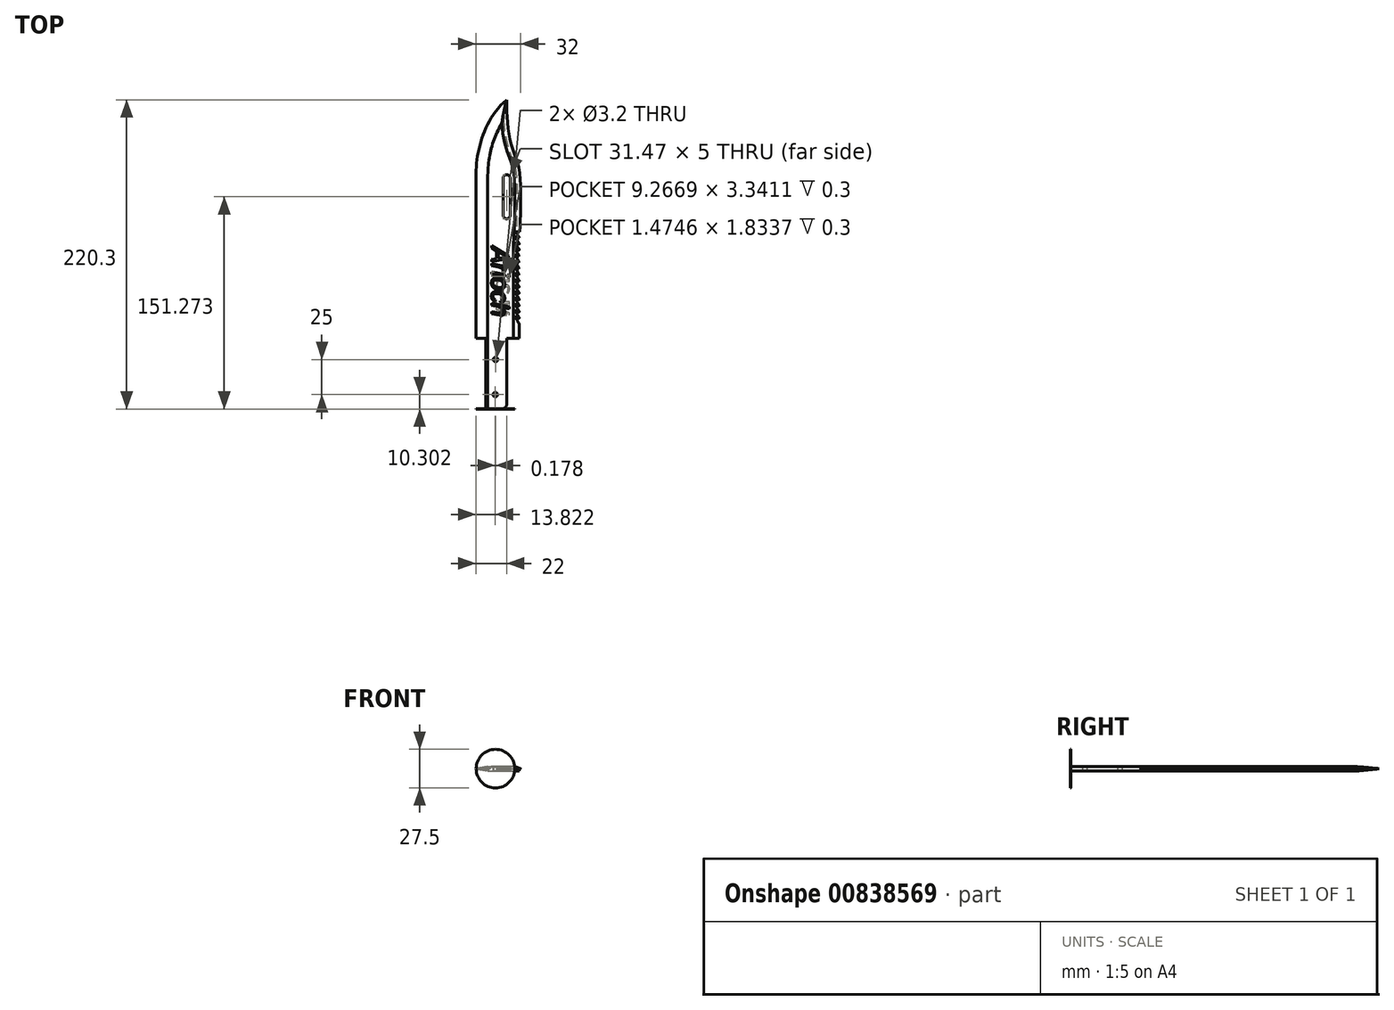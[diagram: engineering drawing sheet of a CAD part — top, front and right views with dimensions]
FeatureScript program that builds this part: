
annotation { "Feature Type Name" : "Feature", "Feature Type Description" : "" }
export const myFeature = defineFeature(function(context is Context, id is Id, definition is map)
    precondition{}
    {
        {
            var Q0;
            Q0=qCreatedBy(makeId("Top.planeOp"),FACE);
            var sketch = newSketch(context, id + "F0", { "sketchPlane" : qUnion([Q0])});
            skLineSegment(sketch, "E0", {"start": v(0, 138.73) * mm, "end": v(0, -81.27) * mm, "construction": true});
            skLineSegment(sketch, "E1", {"start": v(-22, -31.27) * mm, "end": v(9, -31.27) * mm, "construction": true});
            skLineSegment(sketch, "E2", {"start": v(-15, -31.27) * mm, "end": v(-15, -79.27) * mm});
            skLineSegment(sketch, "E3", {"start": v(0, -31.27) * mm, "end": v(0, -78.27) * mm});
            skLineSegment(sketch, "E4", {"start": v(-13, -81.27) * mm, "end": v(-3, -81.27) * mm});
            skPoint(sketch, "E5.visualSharp", {"position": v(0, -81.27) * mm});
            skArc(sketch, "E5.filletArc", {"start": v(-3, -81.27) * mm, "mid": v(-0.88, -80.39) * mm, "end": v(0, -78.27) * mm});
            skPoint(sketch, "E6.visualSharp", {"position": v(-15, -81.27) * mm});
            skArc(sketch, "E6.filletArc", {"start": v(-15, -79.27) * mm, "mid": v(-14.41, -80.68) * mm, "end": v(-13, -81.27) * mm});
            skLineSegment(sketch, "E7", {"start": v(9, -31.27) * mm, "end": v(9, 122.8) * mm, "construction": true});
            skLineSegment(sketch, "E8", {"start": v(-22, -31.27) * mm, "end": v(-22, 123.89) * mm, "construction": true});
            skLineSegment(sketch, "E9", {"start": v(-15, -31.27) * mm, "end": v(-22, -31.27) * mm});
            skLineSegment(sketch, "E10", {"start": v(0, -31.27) * mm, "end": v(9, -31.27) * mm});
            skLineSegment(sketch, "E11", {"start": v(-22, -31.27) * mm, "end": v(-22, 83.23) * mm});
            skFitSpline(sketch, "E12", {"points": [v(-22, 83.23) * mm, v(0, 138.73) * mm], "startDerivative": vector(0, 80.42) * mm, "endDerivative": vector(35.05, 28.76) * mm});
            skFitSpline(sketch, "E13", {"points": [v(0, 138.73) * mm, v(8.64, 90.14) * mm, v(9, 37.85) * mm, v(9, -31.27) * mm], "startDerivative": vector(0, -335.88) * mm, "endDerivative": vector(0, -393.77) * mm});
            skLineSegment(sketch, "E14", {"start": v(-8, -81.27) * mm, "end": v(-8, -31.27) * mm, "construction": true});
            skCircle(sketch, "E15", {"center": v(-8.18, -71.27) * mm, "radius": 1.6 * mm});
            skCircle(sketch, "E16", {"center": v(-8, -46.27) * mm, "radius": 1.6 * mm});
            skSolve(sketch);
        }
        {
            var Q0;
            Q0 = qSketchRegion(id + "F0", true);
            extrude(context, id + "F1", {"entities" : qUnion([Q0]), "depth" : 3 * mm, "offsetDistance" : 25.4 * mm});
        }
        {
            var Q0;
            Q0=makeQuery(id+"F1.opExtrude","CAP_EDGE",EDGE,{"disambiguationData":[OSD([sQuery(id+"F0.wireOp",EDGE,"E11")])],"isStart":false});
            var Q1;
            Q1=makeQuery(id+"F1.opExtrude","CAP_EDGE",EDGE,{"disambiguationData":[OSD([sQuery(id+"F0.wireOp",EDGE,"E12")])],"isStart":false});
            chamfer(context, id + "F2", {"entities" : qUnion([Q0, Q1]), "chamferType" : ChamferType.OFFSET_ANGLE, "width" : 1.5 * mm, "oppositeDirection" : false, "angle" : 80 * degree, "tangentPropagation" : true});
        }
        {
            var Q0;
            Q0=makeQuery(id+"F1.opExtrude","CAP_EDGE",EDGE,{"disambiguationData":[OSD([sQuery(id+"F0.wireOp",EDGE,"E12")])],"isStart":true});
            chamfer(context, id + "F3", {"entities" : qUnion([Q0]), "chamferType" : ChamferType.OFFSET_ANGLE, "width" : 1.5 * mm, "oppositeDirection" : true, "angle" : 80 * degree, "tangentPropagation" : true});
        }
        {
            var Q0;
            Q0=makeQuery(id+"F1.opExtrude","CAP_FACE",FACE,{"disambiguationData":[OSD([sQuery(id+"F0.wireOp",EDGE,"E2"),sQuery(id+"F0.wireOp",EDGE,"E3"),sQuery(id+"F0.wireOp",EDGE,"E4"),sQuery(id+"F0.wireOp",EDGE,"E5.filletArc"),sQuery(id+"F0.wireOp",EDGE,"E6.filletArc"),sQuery(id+"F0.wireOp",EDGE,"E9"),sQuery(id+"F0.wireOp",EDGE,"E10"),sQuery(id+"F0.wireOp",EDGE,"E11"),sQuery(id+"F0.wireOp",EDGE,"E12"),sQuery(id+"F0.wireOp",EDGE,"E13")])],"isStart":true});
            var sketch = newSketch(context, id + "F4", { "sketchPlane" : qUnion([Q0])});
            skSolve(sketch);
        }
        {
            var Q0;
            {var subQ3=sQuery(id+"F0.wireOp",EDGE,"E10");Q0=makeQuery(id+"F4.imprint","IMPRINT",FACE,{"disambiguationData":[TD([[makeQuery(id+"F4.imprint","IMPRINT",EDGE,{"derivedFrom":makeQuery(id+"F1.opExtrude","CAP_EDGE",EDGE,{"disambiguationData":[OSD([subQ3])],"isStart":true})}),-1.0]])]});}
            var sketch = newSketch(context, id + "F5", { "sketchPlane" : qUnion([Q0])});
            skLineSegment(sketch, "E17", {"start": v(10.09, 23.07) * mm, "end": v(6.53, 16.8) * mm});
            skLineSegment(sketch, "E18", {"start": v(6.53, 16.8) * mm, "end": v(10.43, 16.8) * mm});
            skLineSegment(sketch, "E19", {"start": v(10.09, 23.07) * mm, "end": v(10.43, 16.8) * mm});
            skLineSegment(sketch, "E20.0.1.0", {"start": v(10.09, 18.67) * mm, "end": v(10.43, 12.4) * mm});
            skLineSegment(sketch, "E20.0.1.1", {"start": v(6.53, 12.4) * mm, "end": v(10.43, 12.4) * mm});
            skLineSegment(sketch, "E20.0.1.2", {"start": v(10.09, 18.67) * mm, "end": v(6.53, 12.4) * mm});
            skLineSegment(sketch, "E20.0.2.0", {"start": v(10.09, 14.27) * mm, "end": v(10.43, 8) * mm});
            skLineSegment(sketch, "E20.0.2.1", {"start": v(6.53, 8) * mm, "end": v(10.43, 8) * mm});
            skLineSegment(sketch, "E20.0.2.2", {"start": v(10.09, 14.27) * mm, "end": v(6.53, 8) * mm});
            skLineSegment(sketch, "E20.0.3.0", {"start": v(10.09, 9.87) * mm, "end": v(10.43, 3.6) * mm});
            skLineSegment(sketch, "E20.0.3.1", {"start": v(6.53, 3.6) * mm, "end": v(10.43, 3.6) * mm});
            skLineSegment(sketch, "E20.0.3.2", {"start": v(10.09, 9.87) * mm, "end": v(6.53, 3.6) * mm});
            skLineSegment(sketch, "E20.0.4.0", {"start": v(10.09, 5.47) * mm, "end": v(10.43, -0.8) * mm});
            skLineSegment(sketch, "E20.0.4.1", {"start": v(6.53, -0.8) * mm, "end": v(10.43, -0.8) * mm});
            skLineSegment(sketch, "E20.0.4.2", {"start": v(10.09, 5.47) * mm, "end": v(6.53, -0.8) * mm});
            skLineSegment(sketch, "E20.0.5.0", {"start": v(10.09, 1.07) * mm, "end": v(10.43, -5.2) * mm});
            skLineSegment(sketch, "E20.0.5.1", {"start": v(6.53, -5.2) * mm, "end": v(10.43, -5.2) * mm});
            skLineSegment(sketch, "E20.0.5.2", {"start": v(10.09, 1.07) * mm, "end": v(6.53, -5.2) * mm});
            skLineSegment(sketch, "E20.0.6.0", {"start": v(10.09, -3.33) * mm, "end": v(10.43, -9.6) * mm});
            skLineSegment(sketch, "E20.0.6.1", {"start": v(6.53, -9.6) * mm, "end": v(10.43, -9.6) * mm});
            skLineSegment(sketch, "E20.0.6.2", {"start": v(10.09, -3.33) * mm, "end": v(6.53, -9.6) * mm});
            skLineSegment(sketch, "E20.0.7.0", {"start": v(10.09, -7.73) * mm, "end": v(10.43, -14) * mm});
            skLineSegment(sketch, "E20.0.7.1", {"start": v(6.53, -14) * mm, "end": v(10.43, -14) * mm});
            skLineSegment(sketch, "E20.0.7.2", {"start": v(10.09, -7.73) * mm, "end": v(6.53, -14) * mm});
            skLineSegment(sketch, "E20.0.8.0", {"start": v(10.09, -12.13) * mm, "end": v(10.43, -18.4) * mm});
            skLineSegment(sketch, "E20.0.8.1", {"start": v(6.53, -18.4) * mm, "end": v(10.43, -18.4) * mm});
            skLineSegment(sketch, "E20.0.8.2", {"start": v(10.09, -12.13) * mm, "end": v(6.53, -18.4) * mm});
            skLineSegment(sketch, "E20.0.9.0", {"start": v(10.09, -16.53) * mm, "end": v(10.43, -22.8) * mm});
            skLineSegment(sketch, "E20.0.9.1", {"start": v(6.53, -22.8) * mm, "end": v(10.43, -22.8) * mm});
            skLineSegment(sketch, "E20.0.9.2", {"start": v(10.09, -16.53) * mm, "end": v(6.53, -22.8) * mm});
            skLineSegment(sketch, "E20.direction1", {"start": v(6.53, 16.8) * mm, "end": v(32.82, 16.8) * mm, "construction": true});
            skLineSegment(sketch, "E20.direction2", {"start": v(6.53, 16.8) * mm, "end": v(6.53, 12.4) * mm, "construction": true});
            skLineSegment(sketch, "E21.0.0.10", {"start": v(10.09, -20.93) * mm, "end": v(10.43, -27.2) * mm});
            skLineSegment(sketch, "E21.3.0.10", {"start": v(6.53, -27.2) * mm, "end": v(10.43, -27.2) * mm});
            skLineSegment(sketch, "E21.6.0.10", {"start": v(10.09, -20.93) * mm, "end": v(6.53, -27.2) * mm});
            skLineSegment(sketch, "E21.0.0.11", {"start": v(10.09, -25.33) * mm, "end": v(10.43, -31.6) * mm});
            skLineSegment(sketch, "E21.3.0.11", {"start": v(6.53, -31.6) * mm, "end": v(10.43, -31.6) * mm});
            skLineSegment(sketch, "E21.6.0.11", {"start": v(10.09, -25.33) * mm, "end": v(6.53, -31.6) * mm});
            skLineSegment(sketch, "E21.0.0.12", {"start": v(10.09, -29.73) * mm, "end": v(10.43, -36) * mm});
            skLineSegment(sketch, "E21.3.0.12", {"start": v(6.53, -36) * mm, "end": v(10.43, -36) * mm});
            skLineSegment(sketch, "E21.6.0.12", {"start": v(10.09, -29.73) * mm, "end": v(6.53, -36) * mm});
            skLineSegment(sketch, "E21.0.0.13", {"start": v(10.09, -34.13) * mm, "end": v(10.43, -40.4) * mm});
            skLineSegment(sketch, "E21.3.0.13", {"start": v(6.53, -40.4) * mm, "end": v(10.43, -40.4) * mm});
            skLineSegment(sketch, "E21.6.0.13", {"start": v(10.09, -34.13) * mm, "end": v(6.53, -40.4) * mm});
            skLineSegment(sketch, "E21.0.0.14", {"start": v(10.09, -38.53) * mm, "end": v(10.43, -44.8) * mm});
            skLineSegment(sketch, "E21.3.0.14", {"start": v(6.53, -44.8) * mm, "end": v(10.43, -44.8) * mm});
            skLineSegment(sketch, "E21.6.0.14", {"start": v(10.09, -38.53) * mm, "end": v(6.53, -44.8) * mm});
            skSolve(sketch);
        }
        {
            var Q0;
            Q0 = qSketchRegion(id + "F5", true);
            extrude(context, id + "F6", {"entities" : qUnion([Q0]), "operationType" : NewBodyOperationType.REMOVE, "oppositeDirection" : true, "depth" : 25 * mm, "offsetDistance" : 25 * mm});
        }
        {
            var Q0;
            {var subQ3=sQuery(id+"F0.wireOp",EDGE,"E10");Q0=makeQuery(id+"F4.imprint","IMPRINT",FACE,{"disambiguationData":[TD([[makeQuery(id+"F4.imprint","IMPRINT",EDGE,{"derivedFrom":makeQuery(id+"F1.opExtrude","CAP_EDGE",EDGE,{"disambiguationData":[OSD([subQ3])],"isStart":true})}),-1.0]])]});}
            var sketch = newSketch(context, id + "F7", { "sketchPlane" : qUnion([Q0])});
            skLineSegment(sketch, "E22", {"start": v(0, -56.47) * mm, "end": v(0, -82.94) * mm, "construction": true});
            skArc(sketch, "E23.0.startCap", {"start": v(-2.5, -56.47) * mm, "mid": v(0, -53.97) * mm, "end": v(2.5, -56.47) * mm});
            skArc(sketch, "E23.0.endCap", {"start": v(2.5, -82.94) * mm, "mid": v(0, -85.44) * mm, "end": v(-2.5, -82.94) * mm});
            skLineSegment(sketch, "E23.0.left", {"start": v(2.5, -56.47) * mm, "end": v(2.5, -82.94) * mm});
            skLineSegment(sketch, "E23.0.right", {"start": v(-2.5, -56.47) * mm, "end": v(-2.5, -82.94) * mm});
            skSolve(sketch);
        }
        {
            var Q0;
            Q0 = qSketchRegion(id + "F7", true);
            extrude(context, id + "F8", {"entities" : qUnion([Q0]), "operationType" : NewBodyOperationType.REMOVE, "oppositeDirection" : true, "depth" : 25 * mm, "offsetDistance" : 25 * mm});
        }
        {
            var Q0;
            {var subQ0=sQuery(id+"F0.wireOp",EDGE,"E13");var subQ1=sQuery(id+"F0.wireOp",EDGE,"E12");Q0=makeQuery(id+"F6.boolean.opBoolean","SPLIT",EDGE,{"disambiguationData":[TD([makeQuery(id+"F3.opChamfer","BLEND_FACE",FACE,{"disambiguationData":[OSD([subQ1])]})])],"derivedFrom":makeQuery(id+"F1.opExtrude","CAP_EDGE",EDGE,{"disambiguationData":[OSD([subQ0])],"isStart":true})});}
            chamfer(context, id + "F9", {"entities" : qUnion([Q0]), "chamferType" : ChamferType.OFFSET_ANGLE, "width" : 1.5 * mm, "oppositeDirection" : true, "angle" : 60 * degree, "tangentPropagation" : true});
        }
        {
            var Q0;
            {var subQ0=sQuery(id+"F0.wireOp",EDGE,"E13");var subQ1=sQuery(id+"F0.wireOp",EDGE,"E12");Q0=makeQuery(id+"F6.boolean.opBoolean","SPLIT",EDGE,{"disambiguationData":[TD([makeQuery(id+"F2.opChamfer","BLEND_FACE",FACE,{"disambiguationData":[OSD([subQ1])]})])],"derivedFrom":makeQuery(id+"F1.opExtrude","CAP_EDGE",EDGE,{"disambiguationData":[OSD([subQ0])],"isStart":false})});}
            chamfer(context, id + "F10", {"entities" : qUnion([Q0]), "chamferType" : ChamferType.OFFSET_ANGLE, "width" : 1.5 * mm, "oppositeDirection" : false, "angle" : 70 * degree, "tangentPropagation" : true});
        }
        {
            var Q0;
            {var subQ0=sQuery(id+"F0.wireOp",EDGE,"E13");var subQ1=sQuery(id+"F0.wireOp",EDGE,"E12");Q0=makeQuery(id+"F10.opChamfer","BLEND_EDGE",EDGE,{"blendedFrom":[makeQuery(id+"F6.boolean.opBoolean","SPLIT",EDGE,{"disambiguationData":[TD([makeQuery(id+"F2.opChamfer","BLEND_FACE",FACE,{"disambiguationData":[OSD([subQ1])]})])],"derivedFrom":makeQuery(id+"F1.opExtrude","CAP_EDGE",EDGE,{"disambiguationData":[OSD([subQ0])],"isStart":false})}),makeQuery(id+"F6.boolean.opBoolean","COPY",FACE,{"derivedFrom":makeQuery(id+"F6.opExtrude","SWEPT_FACE",FACE,{"disambiguationData":[OSD([sQuery(id+"F5.wireOp",EDGE,"E21.3.0.13")])]})})],"blendedInto":[makeQuery(id+"F6.boolean.opBoolean","COPY",FACE,{"derivedFrom":makeQuery(id+"F6.opExtrude","SWEPT_FACE",FACE,{"disambiguationData":[OSD([sQuery(id+"F5.wireOp",EDGE,"E21.3.0.13")])]})})]});}
            var Q1;
            {var subQ0=sQuery(id+"F0.wireOp",EDGE,"E13");var subQ1=sQuery(id+"F0.wireOp",EDGE,"E12");Q1=makeQuery(id+"F10.opChamfer","BLEND_EDGE",EDGE,{"blendedFrom":[makeQuery(id+"F6.boolean.opBoolean","SPLIT",EDGE,{"disambiguationData":[TD([makeQuery(id+"F2.opChamfer","BLEND_FACE",FACE,{"disambiguationData":[OSD([subQ1])]})])],"derivedFrom":makeQuery(id+"F1.opExtrude","CAP_EDGE",EDGE,{"disambiguationData":[OSD([subQ0])],"isStart":false})}),makeQuery(id+"F6.boolean.opBoolean","COPY",FACE,{"derivedFrom":makeQuery(id+"F6.opExtrude","SWEPT_FACE",FACE,{"disambiguationData":[OSD([sQuery(id+"F5.wireOp",EDGE,"E21.3.0.12")])]})})],"blendedInto":[makeQuery(id+"F6.boolean.opBoolean","COPY",FACE,{"derivedFrom":makeQuery(id+"F6.opExtrude","SWEPT_FACE",FACE,{"disambiguationData":[OSD([sQuery(id+"F5.wireOp",EDGE,"E21.3.0.12")])]})})]});}
            var Q2;
            {var subQ0=sQuery(id+"F0.wireOp",EDGE,"E13");var subQ1=sQuery(id+"F0.wireOp",EDGE,"E12");Q2=makeQuery(id+"F10.opChamfer","BLEND_EDGE",EDGE,{"blendedFrom":[makeQuery(id+"F6.boolean.opBoolean","SPLIT",EDGE,{"disambiguationData":[TD([makeQuery(id+"F2.opChamfer","BLEND_FACE",FACE,{"disambiguationData":[OSD([subQ1])]})])],"derivedFrom":makeQuery(id+"F1.opExtrude","CAP_EDGE",EDGE,{"disambiguationData":[OSD([subQ0])],"isStart":false})}),makeQuery(id+"F6.boolean.opBoolean","COPY",FACE,{"derivedFrom":makeQuery(id+"F6.opExtrude","SWEPT_FACE",FACE,{"disambiguationData":[OSD([sQuery(id+"F5.wireOp",EDGE,"E21.3.0.11")])]})})],"blendedInto":[makeQuery(id+"F6.boolean.opBoolean","COPY",FACE,{"derivedFrom":makeQuery(id+"F6.opExtrude","SWEPT_FACE",FACE,{"disambiguationData":[OSD([sQuery(id+"F5.wireOp",EDGE,"E21.3.0.11")])]})})]});}
            var Q3;
            {var subQ0=sQuery(id+"F0.wireOp",EDGE,"E13");var subQ1=sQuery(id+"F0.wireOp",EDGE,"E12");Q3=makeQuery(id+"F10.opChamfer","BLEND_EDGE",EDGE,{"blendedFrom":[makeQuery(id+"F6.boolean.opBoolean","SPLIT",EDGE,{"disambiguationData":[TD([makeQuery(id+"F2.opChamfer","BLEND_FACE",FACE,{"disambiguationData":[OSD([subQ1])]})])],"derivedFrom":makeQuery(id+"F1.opExtrude","CAP_EDGE",EDGE,{"disambiguationData":[OSD([subQ0])],"isStart":false})}),makeQuery(id+"F6.boolean.opBoolean","COPY",FACE,{"derivedFrom":makeQuery(id+"F6.opExtrude","SWEPT_FACE",FACE,{"disambiguationData":[OSD([sQuery(id+"F5.wireOp",EDGE,"E21.3.0.10")])]})})],"blendedInto":[makeQuery(id+"F6.boolean.opBoolean","COPY",FACE,{"derivedFrom":makeQuery(id+"F6.opExtrude","SWEPT_FACE",FACE,{"disambiguationData":[OSD([sQuery(id+"F5.wireOp",EDGE,"E21.3.0.10")])]})})]});}
            var Q4;
            {var subQ0=sQuery(id+"F0.wireOp",EDGE,"E13");var subQ1=sQuery(id+"F0.wireOp",EDGE,"E12");Q4=makeQuery(id+"F10.opChamfer","BLEND_EDGE",EDGE,{"blendedFrom":[makeQuery(id+"F6.boolean.opBoolean","SPLIT",EDGE,{"disambiguationData":[TD([makeQuery(id+"F2.opChamfer","BLEND_FACE",FACE,{"disambiguationData":[OSD([subQ1])]})])],"derivedFrom":makeQuery(id+"F1.opExtrude","CAP_EDGE",EDGE,{"disambiguationData":[OSD([subQ0])],"isStart":false})}),makeQuery(id+"F6.boolean.opBoolean","COPY",FACE,{"derivedFrom":makeQuery(id+"F6.opExtrude","SWEPT_FACE",FACE,{"disambiguationData":[OSD([sQuery(id+"F5.wireOp",EDGE,"E20.0.9.1")])]})})],"blendedInto":[makeQuery(id+"F6.boolean.opBoolean","COPY",FACE,{"derivedFrom":makeQuery(id+"F6.opExtrude","SWEPT_FACE",FACE,{"disambiguationData":[OSD([sQuery(id+"F5.wireOp",EDGE,"E20.0.9.1")])]})})]});}
            var Q5;
            {var subQ0=sQuery(id+"F0.wireOp",EDGE,"E13");var subQ1=sQuery(id+"F0.wireOp",EDGE,"E12");Q5=makeQuery(id+"F10.opChamfer","BLEND_EDGE",EDGE,{"blendedFrom":[makeQuery(id+"F6.boolean.opBoolean","SPLIT",EDGE,{"disambiguationData":[TD([makeQuery(id+"F2.opChamfer","BLEND_FACE",FACE,{"disambiguationData":[OSD([subQ1])]})])],"derivedFrom":makeQuery(id+"F1.opExtrude","CAP_EDGE",EDGE,{"disambiguationData":[OSD([subQ0])],"isStart":false})}),makeQuery(id+"F6.boolean.opBoolean","COPY",FACE,{"derivedFrom":makeQuery(id+"F6.opExtrude","SWEPT_FACE",FACE,{"disambiguationData":[OSD([sQuery(id+"F5.wireOp",EDGE,"E20.0.8.1")])]})})],"blendedInto":[makeQuery(id+"F6.boolean.opBoolean","COPY",FACE,{"derivedFrom":makeQuery(id+"F6.opExtrude","SWEPT_FACE",FACE,{"disambiguationData":[OSD([sQuery(id+"F5.wireOp",EDGE,"E20.0.8.1")])]})})]});}
            var Q6;
            {var subQ0=sQuery(id+"F0.wireOp",EDGE,"E13");var subQ1=sQuery(id+"F0.wireOp",EDGE,"E12");Q6=makeQuery(id+"F10.opChamfer","BLEND_EDGE",EDGE,{"blendedFrom":[makeQuery(id+"F6.boolean.opBoolean","SPLIT",EDGE,{"disambiguationData":[TD([makeQuery(id+"F2.opChamfer","BLEND_FACE",FACE,{"disambiguationData":[OSD([subQ1])]})])],"derivedFrom":makeQuery(id+"F1.opExtrude","CAP_EDGE",EDGE,{"disambiguationData":[OSD([subQ0])],"isStart":false})}),makeQuery(id+"F6.boolean.opBoolean","COPY",FACE,{"derivedFrom":makeQuery(id+"F6.opExtrude","SWEPT_FACE",FACE,{"disambiguationData":[OSD([sQuery(id+"F5.wireOp",EDGE,"E20.0.7.1")])]})})],"blendedInto":[makeQuery(id+"F6.boolean.opBoolean","COPY",FACE,{"derivedFrom":makeQuery(id+"F6.opExtrude","SWEPT_FACE",FACE,{"disambiguationData":[OSD([sQuery(id+"F5.wireOp",EDGE,"E20.0.7.1")])]})})]});}
            var Q7;
            {var subQ0=sQuery(id+"F0.wireOp",EDGE,"E13");var subQ1=sQuery(id+"F0.wireOp",EDGE,"E12");Q7=makeQuery(id+"F10.opChamfer","BLEND_EDGE",EDGE,{"blendedFrom":[makeQuery(id+"F6.boolean.opBoolean","SPLIT",EDGE,{"disambiguationData":[TD([makeQuery(id+"F2.opChamfer","BLEND_FACE",FACE,{"disambiguationData":[OSD([subQ1])]})])],"derivedFrom":makeQuery(id+"F1.opExtrude","CAP_EDGE",EDGE,{"disambiguationData":[OSD([subQ0])],"isStart":false})}),makeQuery(id+"F6.boolean.opBoolean","COPY",FACE,{"derivedFrom":makeQuery(id+"F6.opExtrude","SWEPT_FACE",FACE,{"disambiguationData":[OSD([sQuery(id+"F5.wireOp",EDGE,"E20.0.6.1")])]})})],"blendedInto":[makeQuery(id+"F6.boolean.opBoolean","COPY",FACE,{"derivedFrom":makeQuery(id+"F6.opExtrude","SWEPT_FACE",FACE,{"disambiguationData":[OSD([sQuery(id+"F5.wireOp",EDGE,"E20.0.6.1")])]})})]});}
            var Q8;
            {var subQ0=sQuery(id+"F0.wireOp",EDGE,"E13");var subQ1=sQuery(id+"F0.wireOp",EDGE,"E12");Q8=makeQuery(id+"F10.opChamfer","BLEND_EDGE",EDGE,{"blendedFrom":[makeQuery(id+"F6.boolean.opBoolean","SPLIT",EDGE,{"disambiguationData":[TD([makeQuery(id+"F2.opChamfer","BLEND_FACE",FACE,{"disambiguationData":[OSD([subQ1])]})])],"derivedFrom":makeQuery(id+"F1.opExtrude","CAP_EDGE",EDGE,{"disambiguationData":[OSD([subQ0])],"isStart":false})}),makeQuery(id+"F6.boolean.opBoolean","COPY",FACE,{"derivedFrom":makeQuery(id+"F6.opExtrude","SWEPT_FACE",FACE,{"disambiguationData":[OSD([sQuery(id+"F5.wireOp",EDGE,"E20.0.5.1")])]})})],"blendedInto":[makeQuery(id+"F6.boolean.opBoolean","COPY",FACE,{"derivedFrom":makeQuery(id+"F6.opExtrude","SWEPT_FACE",FACE,{"disambiguationData":[OSD([sQuery(id+"F5.wireOp",EDGE,"E20.0.5.1")])]})})]});}
            var Q9;
            {var subQ0=sQuery(id+"F0.wireOp",EDGE,"E13");var subQ1=sQuery(id+"F0.wireOp",EDGE,"E12");Q9=makeQuery(id+"F10.opChamfer","BLEND_EDGE",EDGE,{"blendedFrom":[makeQuery(id+"F6.boolean.opBoolean","SPLIT",EDGE,{"disambiguationData":[TD([makeQuery(id+"F2.opChamfer","BLEND_FACE",FACE,{"disambiguationData":[OSD([subQ1])]})])],"derivedFrom":makeQuery(id+"F1.opExtrude","CAP_EDGE",EDGE,{"disambiguationData":[OSD([subQ0])],"isStart":false})}),makeQuery(id+"F6.boolean.opBoolean","COPY",FACE,{"derivedFrom":makeQuery(id+"F6.opExtrude","SWEPT_FACE",FACE,{"disambiguationData":[OSD([sQuery(id+"F5.wireOp",EDGE,"E20.0.4.1")])]})})],"blendedInto":[makeQuery(id+"F6.boolean.opBoolean","COPY",FACE,{"derivedFrom":makeQuery(id+"F6.opExtrude","SWEPT_FACE",FACE,{"disambiguationData":[OSD([sQuery(id+"F5.wireOp",EDGE,"E20.0.4.1")])]})})]});}
            var Q10;
            {var subQ0=sQuery(id+"F0.wireOp",EDGE,"E13");var subQ1=sQuery(id+"F0.wireOp",EDGE,"E12");Q10=makeQuery(id+"F10.opChamfer","BLEND_EDGE",EDGE,{"blendedFrom":[makeQuery(id+"F6.boolean.opBoolean","SPLIT",EDGE,{"disambiguationData":[TD([makeQuery(id+"F2.opChamfer","BLEND_FACE",FACE,{"disambiguationData":[OSD([subQ1])]})])],"derivedFrom":makeQuery(id+"F1.opExtrude","CAP_EDGE",EDGE,{"disambiguationData":[OSD([subQ0])],"isStart":false})}),makeQuery(id+"F6.boolean.opBoolean","COPY",FACE,{"derivedFrom":makeQuery(id+"F6.opExtrude","SWEPT_FACE",FACE,{"disambiguationData":[OSD([sQuery(id+"F5.wireOp",EDGE,"E20.0.3.1")])]})})],"blendedInto":[makeQuery(id+"F6.boolean.opBoolean","COPY",FACE,{"derivedFrom":makeQuery(id+"F6.opExtrude","SWEPT_FACE",FACE,{"disambiguationData":[OSD([sQuery(id+"F5.wireOp",EDGE,"E20.0.3.1")])]})})]});}
            var Q11;
            {var subQ0=sQuery(id+"F0.wireOp",EDGE,"E13");var subQ1=sQuery(id+"F0.wireOp",EDGE,"E12");Q11=makeQuery(id+"F10.opChamfer","BLEND_EDGE",EDGE,{"blendedFrom":[makeQuery(id+"F6.boolean.opBoolean","SPLIT",EDGE,{"disambiguationData":[TD([makeQuery(id+"F2.opChamfer","BLEND_FACE",FACE,{"disambiguationData":[OSD([subQ1])]})])],"derivedFrom":makeQuery(id+"F1.opExtrude","CAP_EDGE",EDGE,{"disambiguationData":[OSD([subQ0])],"isStart":false})}),makeQuery(id+"F6.boolean.opBoolean","COPY",FACE,{"derivedFrom":makeQuery(id+"F6.opExtrude","SWEPT_FACE",FACE,{"disambiguationData":[OSD([sQuery(id+"F5.wireOp",EDGE,"E20.0.2.1")])]})})],"blendedInto":[makeQuery(id+"F6.boolean.opBoolean","COPY",FACE,{"derivedFrom":makeQuery(id+"F6.opExtrude","SWEPT_FACE",FACE,{"disambiguationData":[OSD([sQuery(id+"F5.wireOp",EDGE,"E20.0.2.1")])]})})]});}
            var Q12;
            {var subQ0=sQuery(id+"F0.wireOp",EDGE,"E13");var subQ1=sQuery(id+"F0.wireOp",EDGE,"E12");Q12=makeQuery(id+"F10.opChamfer","BLEND_EDGE",EDGE,{"blendedFrom":[makeQuery(id+"F6.boolean.opBoolean","SPLIT",EDGE,{"disambiguationData":[TD([makeQuery(id+"F2.opChamfer","BLEND_FACE",FACE,{"disambiguationData":[OSD([subQ1])]})])],"derivedFrom":makeQuery(id+"F1.opExtrude","CAP_EDGE",EDGE,{"disambiguationData":[OSD([subQ0])],"isStart":false})}),makeQuery(id+"F6.boolean.opBoolean","COPY",FACE,{"derivedFrom":makeQuery(id+"F6.opExtrude","SWEPT_FACE",FACE,{"disambiguationData":[OSD([sQuery(id+"F5.wireOp",EDGE,"E20.0.1.1")])]})})],"blendedInto":[makeQuery(id+"F6.boolean.opBoolean","COPY",FACE,{"derivedFrom":makeQuery(id+"F6.opExtrude","SWEPT_FACE",FACE,{"disambiguationData":[OSD([sQuery(id+"F5.wireOp",EDGE,"E20.0.1.1")])]})})]});}
            var Q13;
            {var subQ0=sQuery(id+"F0.wireOp",EDGE,"E13");var subQ1=sQuery(id+"F0.wireOp",EDGE,"E12");Q13=makeQuery(id+"F10.opChamfer","BLEND_EDGE",EDGE,{"blendedFrom":[makeQuery(id+"F6.boolean.opBoolean","SPLIT",EDGE,{"disambiguationData":[TD([makeQuery(id+"F2.opChamfer","BLEND_FACE",FACE,{"disambiguationData":[OSD([subQ1])]})])],"derivedFrom":makeQuery(id+"F1.opExtrude","CAP_EDGE",EDGE,{"disambiguationData":[OSD([subQ0])],"isStart":false})}),makeQuery(id+"F6.boolean.opBoolean","COPY",FACE,{"derivedFrom":makeQuery(id+"F6.opExtrude","SWEPT_FACE",FACE,{"disambiguationData":[OSD([sQuery(id+"F5.wireOp",EDGE,"E18")])]})})],"blendedInto":[makeQuery(id+"F6.boolean.opBoolean","COPY",FACE,{"derivedFrom":makeQuery(id+"F6.opExtrude","SWEPT_FACE",FACE,{"disambiguationData":[OSD([sQuery(id+"F5.wireOp",EDGE,"E18")])]})})]});}
            var Q14;
            Q14=makeQuery(id+"F6.boolean.opBoolean","COPY",EDGE,{"derivedFrom":makeQuery(id+"F6.opExtrude","CAP_EDGE",EDGE,{"disambiguationData":[OSD([sQuery(id+"F5.wireOp",EDGE,"E20.0.5.1")])],"isStart":true})});
            var Q15;
            Q15=makeQuery(id+"F6.boolean.opBoolean","COPY",EDGE,{"derivedFrom":makeQuery(id+"F6.opExtrude","CAP_EDGE",EDGE,{"disambiguationData":[OSD([sQuery(id+"F5.wireOp",EDGE,"E20.0.4.1")])],"isStart":true})});
            var Q16;
            Q16=makeQuery(id+"F6.boolean.opBoolean","COPY",EDGE,{"derivedFrom":makeQuery(id+"F6.opExtrude","CAP_EDGE",EDGE,{"disambiguationData":[OSD([sQuery(id+"F5.wireOp",EDGE,"E20.0.3.1")])],"isStart":true})});
            var Q17;
            Q17=makeQuery(id+"F6.boolean.opBoolean","COPY",EDGE,{"derivedFrom":makeQuery(id+"F6.opExtrude","CAP_EDGE",EDGE,{"disambiguationData":[OSD([sQuery(id+"F5.wireOp",EDGE,"E20.0.2.1")])],"isStart":true})});
            var Q18;
            Q18=makeQuery(id+"F6.boolean.opBoolean","COPY",EDGE,{"derivedFrom":makeQuery(id+"F6.opExtrude","CAP_EDGE",EDGE,{"disambiguationData":[OSD([sQuery(id+"F5.wireOp",EDGE,"E20.0.1.1")])],"isStart":true})});
            var Q19;
            Q19=makeQuery(id+"F6.boolean.opBoolean","COPY",EDGE,{"derivedFrom":makeQuery(id+"F6.opExtrude","CAP_EDGE",EDGE,{"disambiguationData":[OSD([sQuery(id+"F5.wireOp",EDGE,"E20.0.6.1")])],"isStart":true})});
            var Q20;
            Q20=makeQuery(id+"F6.boolean.opBoolean","COPY",EDGE,{"derivedFrom":makeQuery(id+"F6.opExtrude","CAP_EDGE",EDGE,{"disambiguationData":[OSD([sQuery(id+"F5.wireOp",EDGE,"E18")])],"isStart":true})});
            var Q21;
            Q21=makeQuery(id+"F6.boolean.opBoolean","COPY",EDGE,{"derivedFrom":makeQuery(id+"F6.opExtrude","CAP_EDGE",EDGE,{"disambiguationData":[OSD([sQuery(id+"F5.wireOp",EDGE,"E20.0.7.1")])],"isStart":true})});
            var Q22;
            Q22=makeQuery(id+"F6.boolean.opBoolean","COPY",EDGE,{"derivedFrom":makeQuery(id+"F6.opExtrude","CAP_EDGE",EDGE,{"disambiguationData":[OSD([sQuery(id+"F5.wireOp",EDGE,"E20.0.8.1")])],"isStart":true})});
            var Q23;
            Q23=makeQuery(id+"F6.boolean.opBoolean","COPY",EDGE,{"derivedFrom":makeQuery(id+"F6.opExtrude","CAP_EDGE",EDGE,{"disambiguationData":[OSD([sQuery(id+"F5.wireOp",EDGE,"E20.0.9.1")])],"isStart":true})});
            var Q24;
            Q24=makeQuery(id+"F6.boolean.opBoolean","COPY",EDGE,{"derivedFrom":makeQuery(id+"F6.opExtrude","CAP_EDGE",EDGE,{"disambiguationData":[OSD([sQuery(id+"F5.wireOp",EDGE,"E21.3.0.10")])],"isStart":true})});
            var Q25;
            Q25=makeQuery(id+"F6.boolean.opBoolean","COPY",EDGE,{"derivedFrom":makeQuery(id+"F6.opExtrude","CAP_EDGE",EDGE,{"disambiguationData":[OSD([sQuery(id+"F5.wireOp",EDGE,"E21.3.0.11")])],"isStart":true})});
            var Q26;
            Q26=makeQuery(id+"F6.boolean.opBoolean","COPY",EDGE,{"derivedFrom":makeQuery(id+"F6.opExtrude","CAP_EDGE",EDGE,{"disambiguationData":[OSD([sQuery(id+"F5.wireOp",EDGE,"E21.3.0.12")])],"isStart":true})});
            var Q27;
            Q27=makeQuery(id+"F6.boolean.opBoolean","COPY",EDGE,{"derivedFrom":makeQuery(id+"F6.opExtrude","CAP_EDGE",EDGE,{"disambiguationData":[OSD([sQuery(id+"F5.wireOp",EDGE,"E21.3.0.13")])],"isStart":true})});
            chamfer(context, id + "F11", {"entities" : qUnion([Q0, Q1, Q2, Q3, Q4, Q5, Q6, Q7, Q8, Q9, Q10, Q11, Q12, Q13, Q14, Q15, Q16, Q17, Q18, Q19, Q20, Q21, Q22, Q23, Q24, Q25, Q26, Q27]), "chamferType" : ChamferType.OFFSET_ANGLE, "width" : 0.9 * mm, "oppositeDirection" : false, "angle" : 45 * degree});
        }
        {
            var Q0;
            {var subQ3=sQuery(id+"F0.wireOp",EDGE,"E10");Q0=makeQuery(id+"F4.imprint","IMPRINT",FACE,{"disambiguationData":[TD([[makeQuery(id+"F4.imprint","IMPRINT",EDGE,{"derivedFrom":makeQuery(id+"F1.opExtrude","CAP_EDGE",EDGE,{"disambiguationData":[OSD([subQ3])],"isStart":true})}),-1.0]])]});}
            var sketch = newSketch(context, id + "F12", { "sketchPlane" : qUnion([Q0])});
            skText(sketch, "E24", { "text": "M-25", "fontName": "NotoSans-Regular.ttf"});
            const initialGuessF12  = {"E24": [-0.0076, 0.01609, 0, -1, 0.00964]};
            skSetInitialGuess(sketch, initialGuessF12);
            skSolve(sketch);
        }
        {
            var Q0;
            Q0 = qSketchRegion(id + "F12", true);
            extrude(context, id + "F13", {"entities" : qUnion([Q0]), "operationType" : NewBodyOperationType.REMOVE, "oppositeDirection" : true, "depth" : 0.3 * mm, "offsetDistance" : 25 * mm});
        }
        {
            var Q0;
            Q0=makeQuery(id+"F1.opExtrude","CAP_FACE",FACE,{"disambiguationData":[OSD([sQuery(id+"F0.wireOp",EDGE,"E2"),sQuery(id+"F0.wireOp",EDGE,"E3"),sQuery(id+"F0.wireOp",EDGE,"E4"),sQuery(id+"F0.wireOp",EDGE,"E5.filletArc"),sQuery(id+"F0.wireOp",EDGE,"E6.filletArc"),sQuery(id+"F0.wireOp",EDGE,"E9"),sQuery(id+"F0.wireOp",EDGE,"E10"),sQuery(id+"F0.wireOp",EDGE,"E11"),sQuery(id+"F0.wireOp",EDGE,"E12"),sQuery(id+"F0.wireOp",EDGE,"E13"),sQuery(id+"F0.wireOp",EDGE,"E15"),sQuery(id+"F0.wireOp",EDGE,"E16")])],"isStart":false});
            var sketch = newSketch(context, id + "F14", { "sketchPlane" : qUnion([Q0])});
            skText(sketch, "E25", { "text": "Arioch", "fontName": "Arimo-Italic.ttf"});
            const initialGuessF14  = {"E25": [-0.0108, 0.03404, 0, -1, 0.01263]};
            skSetInitialGuess(sketch, initialGuessF14);
            skSolve(sketch);
        }
        {
            var Q0;
            Q0 = qSketchRegion(id + "F14", true);
            extrude(context, id + "F15", {"entities" : qUnion([Q0]), "operationType" : NewBodyOperationType.REMOVE, "oppositeDirection" : true, "depth" : 0.3 * mm, "offsetDistance" : 25 * mm});
        }
        {
            var Q0;
            Q0=makeQuery(id+"F1.opExtrude","SWEPT_FACE",FACE,{"disambiguationData":[OSD([sQuery(id+"F0.wireOp",EDGE,"E4")])]});
            var sketch = newSketch(context, id + "F16", { "sketchPlane" : qUnion([Q0])});
            skCircle(sketch, "E26", {"center": v(-8, 1.53) * mm, "radius": 13.75 * mm});
            skPoint(sketch, "E26.centerSnap0", {"position": v(-8, 3) * mm});
            skSolve(sketch);
        }
        {
            var Q0;
            Q0 = qSketchRegion(id + "F16", true);
            extrude(context, id + "F17", {"entities" : qUnion([Q0]), "operationType" : NewBodyOperationType.ADD, "depth" : 0.3 * mm, "offsetDistance" : 25 * mm});
        }
    });
